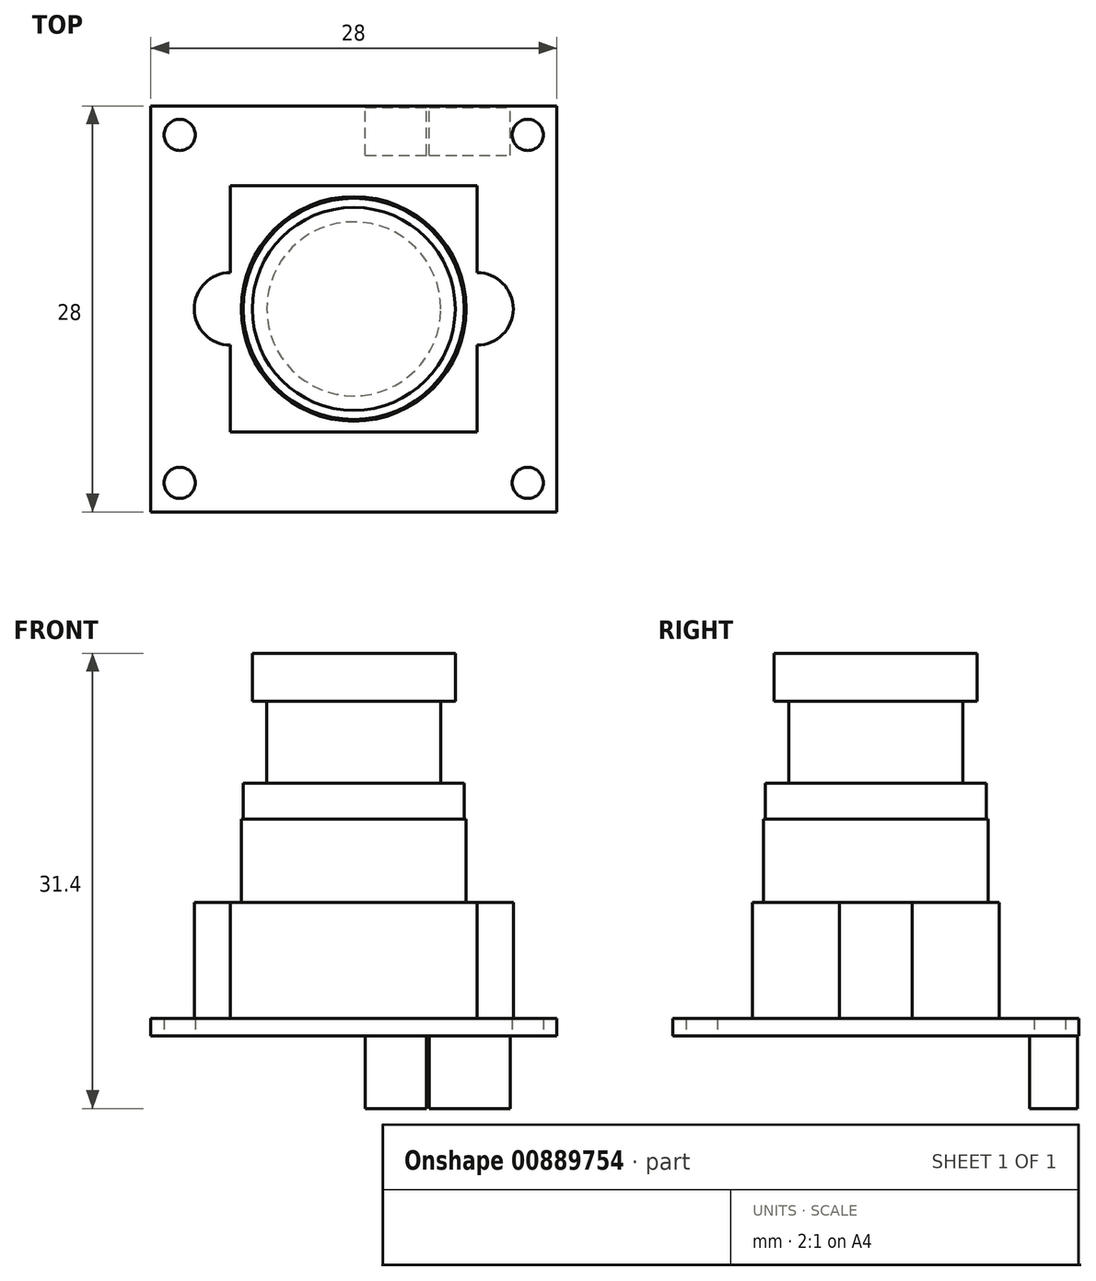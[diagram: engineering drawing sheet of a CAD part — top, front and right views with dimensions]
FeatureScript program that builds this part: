
annotation { "Feature Type Name" : "Feature", "Feature Type Description" : "" }
export const myFeature = defineFeature(function(context is Context, id is Id, definition is map)
    precondition{}
    {
        {
            var Q0;
            Q0=qCreatedBy(makeId("Top.planeOp"),FACE);
            var sketch = newSketch(context, id + "F0", { "sketchPlane" : qUnion([Q0])});
            skLineSegment(sketch, "E0.bottom", {"start": v(-14, 14) * mm, "end": v(14, 14) * mm});
            skLineSegment(sketch, "E0.top", {"start": v(-14, -14) * mm, "end": v(14, -14) * mm});
            skLineSegment(sketch, "E0.left", {"start": v(-14, 14) * mm, "end": v(-14, -14) * mm});
            skLineSegment(sketch, "E0.right", {"start": v(14, 14) * mm, "end": v(14, -14) * mm});
            skLineSegment(sketch, "E1", {"start": v(-14, 14) * mm, "end": v(14, -14) * mm, "construction": true});
            skCircle(sketch, "E2", {"center": v(-12, 12) * mm, "radius": 1.07 * mm});
            skCircle(sketch, "E3.1.0", {"center": v(-12, -12) * mm, "radius": 1.07 * mm});
            skCircle(sketch, "E3.2.0", {"center": v(12, -12) * mm, "radius": 1.07 * mm});
            skCircle(sketch, "E3.3.0", {"center": v(12, 12) * mm, "radius": 1.07 * mm});
            skPoint(sketch, "E3.center", {"position": v(0, 0) * mm});
            skSolve(sketch);
        }
        {
            var Q0;
            Q0=qSketchRegion(id+"F0",true);
            extrude(context, id + "F1", {"entities" : qUnion([Q0]), "depth" : 1.2 * mm});
        }
        {
            var Q0;
            Q0=makeQuery(id+"F1.opExtrude","CAP_FACE",FACE,{"disambiguationData":[OSD([sQuery(id+"F0.wireOp",EDGE,"E0.bottom"),sQuery(id+"F0.wireOp",EDGE,"E0.top"),sQuery(id+"F0.wireOp",EDGE,"E0.left"),sQuery(id+"F0.wireOp",EDGE,"E0.right"),sQuery(id+"F0.wireOp",EDGE,"E2"),sQuery(id+"F0.wireOp",EDGE,"E3.1.0"),sQuery(id+"F0.wireOp",EDGE,"E3.2.0"),sQuery(id+"F0.wireOp",EDGE,"E3.3.0")])],"isStart":false});
            var sketch = newSketch(context, id + "F2", { "sketchPlane" : qUnion([Q0])});
            skLineSegment(sketch, "E4.bottom", {"start": v(-8.5, 8.5) * mm, "end": v(8.5, 8.5) * mm});
            skLineSegment(sketch, "E4.top", {"start": v(-8.5, -8.5) * mm, "end": v(8.5, -8.5) * mm});
            skLineSegment(sketch, "E4.left", {"start": v(-8.5, 8.5) * mm, "end": v(-8.5, 2.5) * mm});
            skLineSegment(sketch, "E4.right", {"start": v(8.5, 8.5) * mm, "end": v(8.5, 2.5) * mm});
            skArc(sketch, "E5", {"start": v(-8.5, 2.5) * mm, "mid": v(-11, 0) * mm, "end": v(-8.5, -2.5) * mm});
            skArc(sketch, "E6", {"start": v(8.5, -2.5) * mm, "mid": v(11, 0) * mm, "end": v(8.5, 2.5) * mm});
            skLineSegment(sketch, "E7.trimOffspring", {"start": v(-8.5, -2.5) * mm, "end": v(-8.5, -8.5) * mm});
            skLineSegment(sketch, "E8.trimOffspring", {"start": v(8.5, -2.5) * mm, "end": v(8.5, -8.5) * mm});
            skSolve(sketch);
        }
        {
            var Q0;
            Q0=makeQuery(id+"F2.imprint","IMPRINT",FACE,{"disambiguationData":[TD([[makeQuery(id+"F2.imprint","IMPRINT",EDGE,{"derivedFrom":sQuery(id+"F2.wireOp",EDGE,"E4.bottom")}),-1.0]])]});
            extrude(context, id + "F3", {"entities" : qUnion([Q0]), "depth" : 8 * mm});
        }
        {
            var Q0;
            Q0=qCreatedBy(makeId("Front.planeOp"),FACE);
            var sketch = newSketch(context, id + "F4", { "sketchPlane" : qUnion([Q0])});
            skLineSegment(sketch, "E9", {"start": v(0, 26.4) * mm, "end": v(-7, 26.4) * mm});
            skLineSegment(sketch, "E10", {"start": v(-7, 26.4) * mm, "end": v(-7, 23.1) * mm});
            skLineSegment(sketch, "E11", {"start": v(-7, 23.1) * mm, "end": v(-6, 23.1) * mm});
            skLineSegment(sketch, "E12", {"start": v(-6, 23.1) * mm, "end": v(-6, 17.45) * mm});
            skLineSegment(sketch, "E13", {"start": v(-6, 17.45) * mm, "end": v(-7.62, 17.45) * mm});
            skLineSegment(sketch, "E14", {"start": v(-7.62, 17.45) * mm, "end": v(-7.62, 14.95) * mm});
            skLineSegment(sketch, "E15", {"start": v(-7.62, 14.95) * mm, "end": v(-7.75, 14.95) * mm});
            skLineSegment(sketch, "E16", {"start": v(-7.75, 14.95) * mm, "end": v(-7.75, 9.2) * mm});
            skLineSegment(sketch, "E17", {"start": v(0, 9.2) * mm, "end": v(0, 26.4) * mm});
            skLineSegment(sketch, "E18.0", {"start": v(-7.75, 9.2) * mm, "end": v(0, 9.2) * mm});
            skSolve(sketch);
        }
        {
            var Q0;
            Q0=makeQuery(id+"F4.imprint","IMPRINT",FACE,{"disambiguationData":[TD([[makeQuery(id+"F4.imprint","IMPRINT",EDGE,{"derivedFrom":sQuery(id+"F4.wireOp",EDGE,"E9")}),1.0]])]});
            var Q1;
            Q1=sQuery(id+"F4.wireOp",EDGE,"E17");
            revolve(context, id + "F5", {"operationType" : NewBodyOperationType.ADD, "entities" : qUnion([Q0]), "axis" : qUnion([Q1]), "revolveType" : RevolveType.FULL});
        }
        {
            var Q0;
            Q0=makeQuery(id+"F1.opExtrude","CAP_FACE",FACE,{"disambiguationData":[OSD([sQuery(id+"F0.wireOp",EDGE,"E0.bottom"),sQuery(id+"F0.wireOp",EDGE,"E0.top"),sQuery(id+"F0.wireOp",EDGE,"E0.left"),sQuery(id+"F0.wireOp",EDGE,"E0.right"),sQuery(id+"F0.wireOp",EDGE,"E2"),sQuery(id+"F0.wireOp",EDGE,"E3.1.0"),sQuery(id+"F0.wireOp",EDGE,"E3.2.0"),sQuery(id+"F0.wireOp",EDGE,"E3.3.0")])],"isStart":true});
            var sketch = newSketch(context, id + "F6", { "sketchPlane" : qUnion([Q0])});
            skLineSegment(sketch, "E19.bottom", {"start": v(0.8, -10.6) * mm, "end": v(5, -10.6) * mm});
            skLineSegment(sketch, "E19.top", {"start": v(0.8, -13.9) * mm, "end": v(5, -13.9) * mm});
            skLineSegment(sketch, "E19.left", {"start": v(0.8, -10.6) * mm, "end": v(0.8, -13.9) * mm});
            skLineSegment(sketch, "E19.right", {"start": v(5, -10.6) * mm, "end": v(5, -13.9) * mm});
            skLineSegment(sketch, "E20.bottom", {"start": v(5.2, -10.6) * mm, "end": v(10.8, -10.6) * mm});
            skLineSegment(sketch, "E20.top", {"start": v(5.2, -13.9) * mm, "end": v(10.8, -13.9) * mm});
            skLineSegment(sketch, "E20.left", {"start": v(5.2, -10.6) * mm, "end": v(5.2, -13.9) * mm});
            skLineSegment(sketch, "E20.right", {"start": v(10.8, -10.6) * mm, "end": v(10.8, -13.9) * mm});
            skSolve(sketch);
        }
        {
            var Q0;
            Q0=qSketchRegion(id+"F6",true);
            extrude(context, id + "F7", {"entities" : qUnion([Q0]), "operationType" : NewBodyOperationType.ADD, "depth" : 5 * mm});
        }
    });
